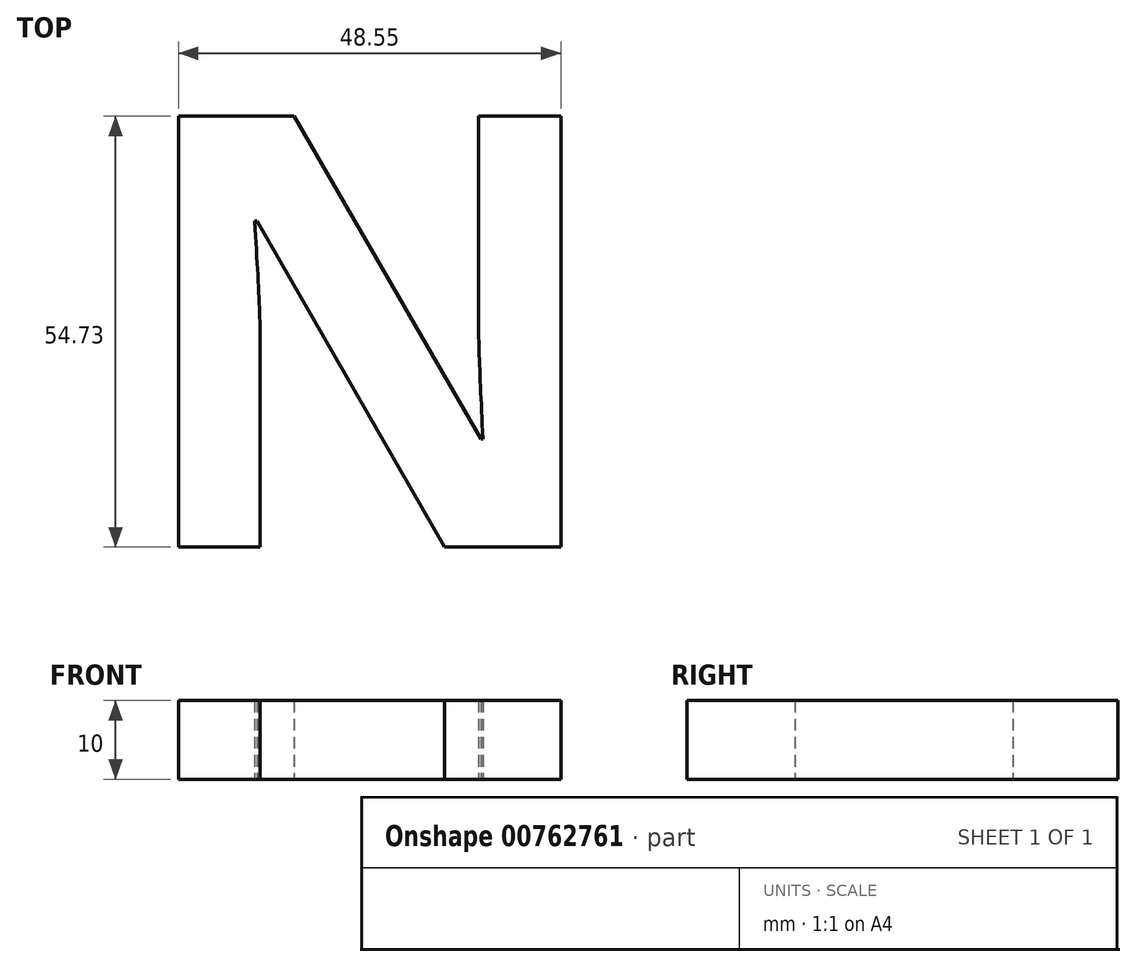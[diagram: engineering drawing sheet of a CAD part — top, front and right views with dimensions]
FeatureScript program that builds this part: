
annotation { "Feature Type Name" : "Feature", "Feature Type Description" : "" }
export const myFeature = defineFeature(function(context is Context, id is Id, definition is map)
    precondition{}
    {
        {
            var Q0;
            Q0=qCreatedBy(makeId("Top.planeOp"),FACE);
            var sketch = newSketch(context, id + "F0", { "sketchPlane" : qUnion([Q0])});
            skText(sketch, "E0", { "text": "N", "fontName": "OpenSans-Bold.ttf"});
            const initialGuessF0  = {"E0": [0, 0, 1, 0, 0.0552]};
            skSetInitialGuess(sketch, initialGuessF0);
            skSolve(sketch);
        }
        {
            var Q0;
            Q0 = qSketchRegion(id + "F0", true);
            extrude(context, id + "F1", {"entities" : qUnion([Q0]), "depth" : 10 * mm, "offsetDistance" : 25 * mm});
        }
    });
